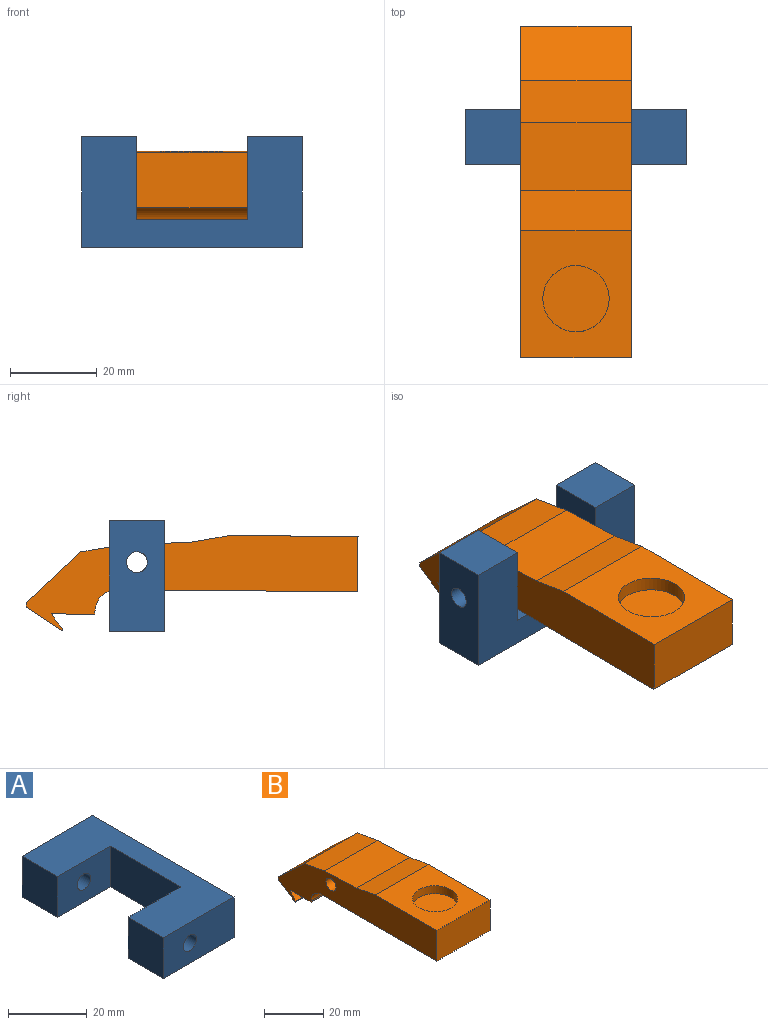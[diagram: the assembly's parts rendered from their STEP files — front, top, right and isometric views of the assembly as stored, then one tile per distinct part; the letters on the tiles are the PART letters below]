
ASSEMBLY  parts=2 mates=1
PART A: 12 faces, bbox 25.4x50.8x12.7 mm
  f0: plane 12.7x12.7mm, normal (-1,0,0), area 161.3mm2, adj f1,f7,f8,f9
  f1: plane 19.05x12.7mm, normal (0,-1,0), area 223.6mm2, adj f0,f2,f8,f9,f10
  f2: plane 25.4x12.7mm, normal (-1,0,0), area 322.6mm2, adj f1,f3,f8,f9
  f3: plane 19.05x12.7mm, normal (0,1,0), area 223.6mm2, adj f2,f4,f8,f9,f11
  f4: plane 12.7x12.7mm, normal (-1,0,0), area 161.3mm2, adj f3,f5,f8,f9
  f5: plane 25.4x12.7mm, normal (0,-1,0), area 304.3mm2, adj f4,f6,f8,f9,f11
  f6: plane 50.8x12.7mm, normal (1,0,0), area 645.2mm2, adj f5,f7,f8,f9
  f7: plane 25.4x12.7mm, normal (0,1,0), area 304.3mm2, adj f0,f6,f8,f9,f10
  f8: plane 50.8x25.4mm, normal (0,0,1), area 806.4mm2, adj f0,f1,f2,f3,f4,f5,f6,f7
  f9: plane 50.8x25.4mm, normal (0,0,-1), area 806.4mm2, adj f0,f1,f2,f3,f4,f5,f6,f7
  f10: cylinder r=2.41mm len=12.7mm, axis (0,-1,0), area 192.5mm2, adj f1,f7
  f11: cylinder r=2.41mm len=12.7mm, axis (0,-1,0), area 192.5mm2, adj f3,f5
PART B: 19 faces, bbox 25.4x76.2x22.2 mm
  f0: plane 25.4x1.06mm, normal (0,1,0), area 27mm2, adj f1,f2,f17,f18
  f1: plane 76.2x22.23mm, normal (-1,0,0), area 856.3mm2, adj f0,f3,f4,f5,f6,f9,f10,f11
  f2: plane 76.2x22.23mm, normal (1,0,0), area 856.3mm2, adj f0,f3,f4,f5,f6,f9,f10,f11
  f3: plane 25.4x12.7mm, normal (0,-1,0), area 322.6mm2, adj f1,f2,f4,f5
  f4: plane 29.42x25.4mm, normal (0,0,1), area 564.9mm2, adj f1,f2,f3,f7,f9
  f5: plane 55.26x25.4mm, normal (0,0,-1), area 1403.5mm2, adj f1,f2,f3,f15
  f6: cylinder r=2.41mm len=25.4mm, axis (1,0,0), area 385.1mm2, adj f1,f2
  f7: cylinder r=7.62mm len=15.24mm, axis (0,0,1), area 158.1mm2, adj f4,f8
  f8: plane 15.24x15.24mm, normal (0,0,1), area 182.4mm2, adj f7
  f9: plane 25.4x9.02mm, normal (0,0.18,0.98), area 232.9mm2, adj f1,f2,f4,f10
  f10: plane 25.4x15.65mm, normal (0,0.05,1), area 397.9mm2, adj f1,f2,f9,f11
  f11: plane 25.4x9.61mm, normal (0,0.18,0.98), area 248.1mm2, adj f1,f2,f10,f17
  f12: plane 25.4x0.64mm, normal (0,-1,0), area 16.1mm2, adj f1,f2,f13,f15
  f13: plane 25.4x9.98mm, normal (0,0,-1), area 253.4mm2, adj f1,f2,f12,f14
  f14: cylinder r=22.94mm len=25.4mm, axis (1,0,0), area 107.9mm2, adj f1,f2,f13,f16
  f15: cylinder r=5.08mm len=25.4mm, axis (1,0,0), area 202.7mm2, adj f1,f2,f5,f12
  f16: cylinder r=0.25mm len=25.4mm, axis (1,0,0), area 14.9mm2, adj f1,f2,f14,f18
  f17: plane 25.4x12.5mm, normal (0,0.69,0.73), area 436.1mm2, adj f0,f1,f2,f11
  f18: plane 25.4x8.26mm, normal (0,0.54,-0.84), area 249mm2, adj f0,f1,f2,f16
PLACE A rot(axis=(0.58,0.58,-0.58),120deg) t=(-37.64,66.32,-1.9)mm
PLACE B rot(axis=(1,0,0),0.5deg) t=(-24.94,9.24,-18.25)mm
MATE revolute B.f14 <-> A.f10  axis (1,0,0) through (-12.24,59.98,-11.43)mm
